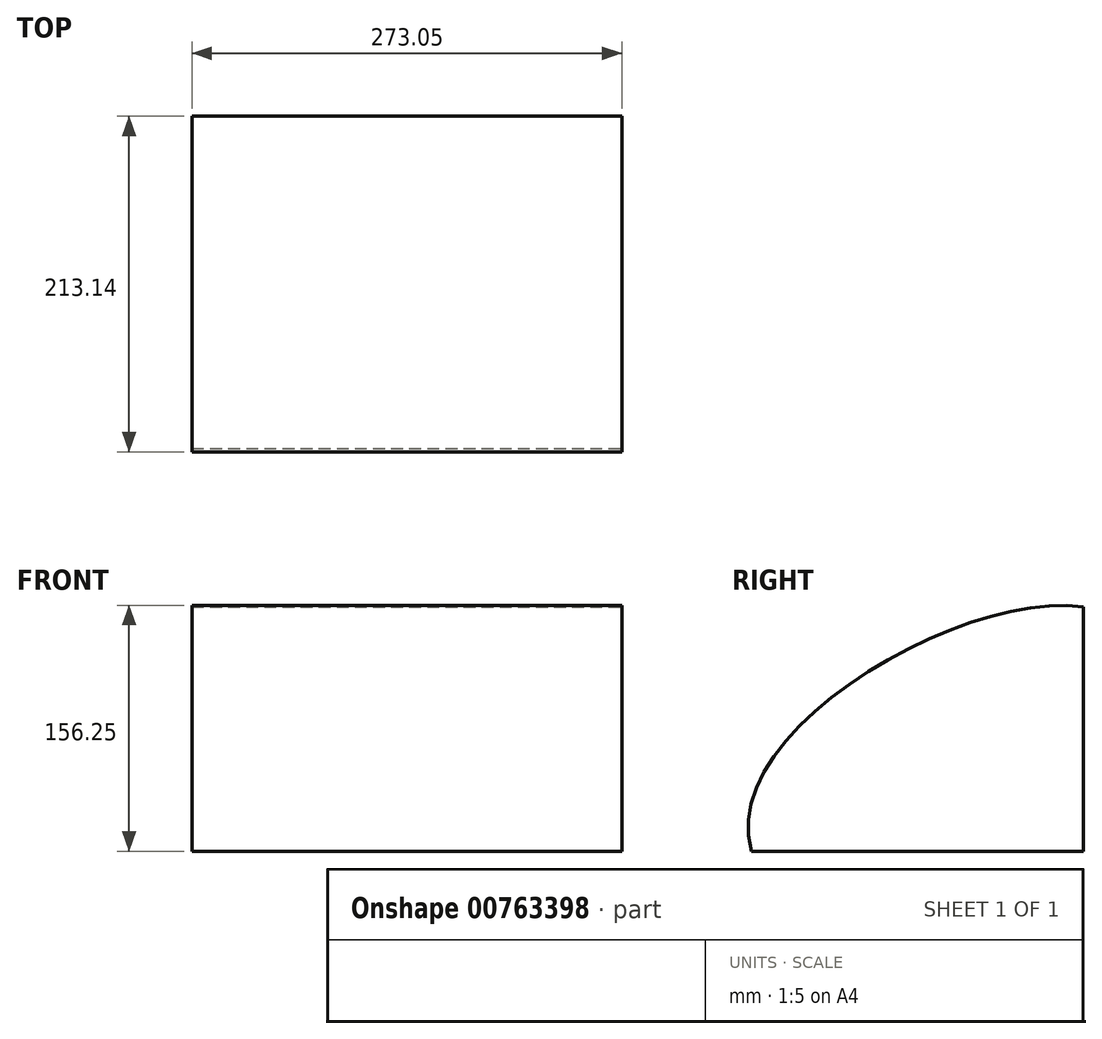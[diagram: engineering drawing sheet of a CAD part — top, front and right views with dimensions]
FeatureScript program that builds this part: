
annotation { "Feature Type Name" : "Feature", "Feature Type Description" : "" }
export const myFeature = defineFeature(function(context is Context, id is Id, definition is map)
    precondition{}
    {
        {
            var Q0;
            Q0=qCreatedBy(makeId("Right.planeOp"),FACE);
            var sketch = newSketch(context, id + "F0", { "sketchPlane" : qUnion([Q0])});
            skLineSegment(sketch, "E0", {"start": v(-109.75, -56.17) * mm, "end": v(101.24, -56.17) * mm});
            skLineSegment(sketch, "E1", {"start": v(101.24, -56.17) * mm, "end": v(101.24, 99.18) * mm});
            skFitSpline(sketch, "E2", {"points": [v(101.24, 99.18) * mm, v(-109.75, -56.17) * mm], "startDerivative": vector(-230.67, 32.8) * mm, "endDerivative": vector(66.81, -227.42) * mm});
            skSolve(sketch);
        }
        {
            var Q0;
            Q0 = qSketchRegion(id + "F0", true);
            extrude(context, id + "F1", {"entities" : qUnion([Q0]), "oppositeDirection" : true, "depth" : 273.05 * mm, "offsetDistance" : 25.4 * mm});
        }
    });
